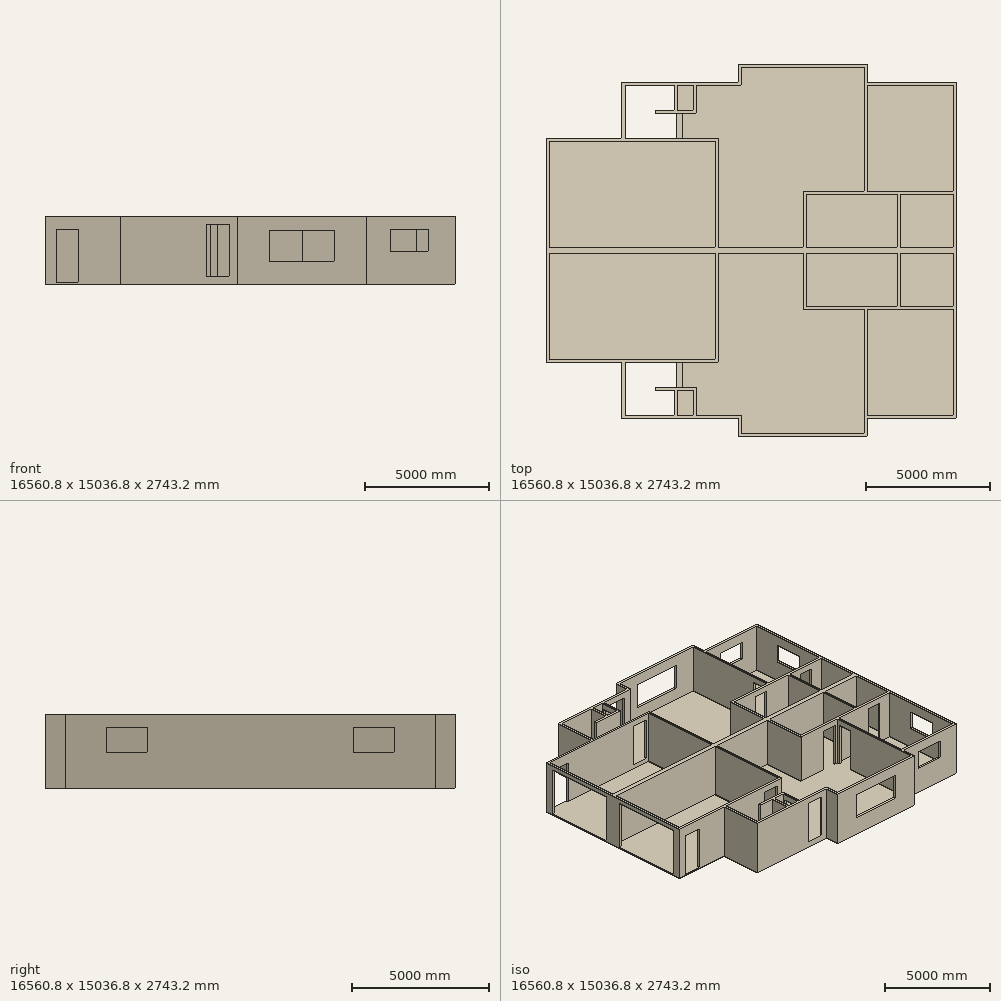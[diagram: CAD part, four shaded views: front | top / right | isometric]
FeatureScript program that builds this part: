
annotation { "Feature Type Name" : "Feature", "Feature Type Description" : "" }
export const myFeature = defineFeature(function(context is Context, id is Id, definition is map)
    precondition{}
    {
        {
            var Q0;
            Q0=qCreatedBy(makeId("Top.planeOp"),FACE);
            var sketch = newSketch(context, id + "F0", { "sketchPlane" : qUnion([Q0])});
            skLineSegment(sketch, "E0", {"start": v(0, 0) * mm, "end": v(16560.8, 0) * mm});
            skLineSegment(sketch, "E1", {"start": v(0, 0) * mm, "end": v(0, 4521.2) * mm});
            skLineSegment(sketch, "E2", {"start": v(0, 4521.2) * mm, "end": v(3048, 4521.2) * mm});
            skLineSegment(sketch, "E3", {"start": v(3048, 4521.2) * mm, "end": v(3048, 6781.8) * mm});
            skLineSegment(sketch, "E4", {"start": v(3048, 6781.8) * mm, "end": v(7747, 6781.8) * mm});
            skLineSegment(sketch, "E5", {"start": v(7747, 6781.8) * mm, "end": v(7747, 7518.4) * mm});
            skLineSegment(sketch, "E6", {"start": v(7747, 7518.4) * mm, "end": v(12979.4, 7518.4) * mm});
            skLineSegment(sketch, "E7", {"start": v(12979.4, 7518.4) * mm, "end": v(12979.4, 6781.8) * mm});
            skLineSegment(sketch, "E8", {"start": v(12979.4, 6781.8) * mm, "end": v(16560.8, 6781.8) * mm});
            skLineSegment(sketch, "E9", {"start": v(16560.8, 6781.8) * mm, "end": v(16560.8, 0) * mm});
            skSolve(sketch);
        }
        {
            var Q0;
            Q0 = qSketchRegion(id + "F0", true);
            extrude(context, id + "F1", {"entities" : qUnion([Q0]), "depth" : 2743.2 * mm});
        }
        {
            var Q0;
            Q0=makeQuery(id+"F1.opExtrude","CAP_FACE",FACE,{"disambiguationData":[OSD([sQuery(id+"F0.wireOp",EDGE,"E0"),sQuery(id+"F0.wireOp",EDGE,"E1"),sQuery(id+"F0.wireOp",EDGE,"E2"),sQuery(id+"F0.wireOp",EDGE,"E3"),sQuery(id+"F0.wireOp",EDGE,"E4"),sQuery(id+"F0.wireOp",EDGE,"E5"),sQuery(id+"F0.wireOp",EDGE,"E6"),sQuery(id+"F0.wireOp",EDGE,"E7"),sQuery(id+"F0.wireOp",EDGE,"E8"),sQuery(id+"F0.wireOp",EDGE,"E9")])],"isStart":false});
            var sketch = newSketch(context, id + "F2", { "sketchPlane" : qUnion([Q0])});
            skLineSegment(sketch, "E10.bottom", {"start": v(127, 4394.2) * mm, "end": v(6832.6, 4394.2) * mm});
            skLineSegment(sketch, "E10.top", {"start": v(127, 127) * mm, "end": v(6832.6, 127) * mm});
            skLineSegment(sketch, "E10.left", {"start": v(127, 4394.2) * mm, "end": v(127, 127) * mm});
            skLineSegment(sketch, "E10.right", {"start": v(6832.6, 4394.2) * mm, "end": v(6832.6, 127) * mm});
            skLineSegment(sketch, "E11.bottom", {"start": v(16433.8, 6654.8) * mm, "end": v(12979.4, 6654.8) * mm});
            skLineSegment(sketch, "E11.top", {"start": v(16433.8, 2387.6) * mm, "end": v(12979.4, 2387.6) * mm});
            skLineSegment(sketch, "E11.left", {"start": v(16433.8, 6654.8) * mm, "end": v(16433.8, 2387.6) * mm});
            skLineSegment(sketch, "E11.right", {"start": v(12979.4, 6654.8) * mm, "end": v(12979.4, 2387.6) * mm});
            skLineSegment(sketch, "E12.bottom", {"start": v(16433.8, 2260.6) * mm, "end": v(14300.2, 2260.6) * mm});
            skLineSegment(sketch, "E12.top", {"start": v(16433.8, 127) * mm, "end": v(14300.2, 127) * mm});
            skLineSegment(sketch, "E12.left", {"start": v(16433.8, 2260.6) * mm, "end": v(16433.8, 127) * mm});
            skLineSegment(sketch, "E12.right", {"start": v(14300.2, 2260.6) * mm, "end": v(14300.2, 127) * mm});
            skLineSegment(sketch, "E13.bottom", {"start": v(14173.2, 127) * mm, "end": v(10515.6, 127) * mm});
            skLineSegment(sketch, "E13.top", {"start": v(14173.2, 2260.6) * mm, "end": v(10515.6, 2260.6) * mm});
            skLineSegment(sketch, "E13.left", {"start": v(14173.2, 127) * mm, "end": v(14173.2, 2260.6) * mm});
            skLineSegment(sketch, "E13.right", {"start": v(10515.6, 127) * mm, "end": v(10515.6, 2260.6) * mm});
            skLineSegment(sketch, "E14", {"start": v(6959.6, 4521.2) * mm, "end": v(6959.6, 127) * mm});
            skLineSegment(sketch, "E15", {"start": v(6959.6, 127) * mm, "end": v(10388.6, 127) * mm});
            skLineSegment(sketch, "E16", {"start": v(10388.6, 127) * mm, "end": v(10388.6, 2387.6) * mm});
            skLineSegment(sketch, "E17", {"start": v(10388.6, 2387.6) * mm, "end": v(12852.4, 2387.6) * mm});
            skLineSegment(sketch, "E18", {"start": v(12852.4, 2387.6) * mm, "end": v(12852.4, 7391.4) * mm});
            skLineSegment(sketch, "E19", {"start": v(12852.4, 7391.4) * mm, "end": v(7874, 7391.4) * mm});
            skLineSegment(sketch, "E20", {"start": v(7874, 7391.4) * mm, "end": v(7874, 6654.8) * mm});
            skLineSegment(sketch, "E21", {"start": v(7874, 6654.8) * mm, "end": v(6045.2, 6654.8) * mm});
            skLineSegment(sketch, "E22", {"start": v(6045.2, 6654.8) * mm, "end": v(6045.2, 5524.5) * mm});
            skLineSegment(sketch, "E23", {"start": v(3175, 6654.8) * mm, "end": v(3175, 4521.2) * mm});
            skLineSegment(sketch, "E24", {"start": v(3175, 4521.2) * mm, "end": v(6959.6, 4521.2) * mm});
            skLineSegment(sketch, "E25", {"start": v(3175, 6654.8) * mm, "end": v(5181.6, 6654.8) * mm});
            skLineSegment(sketch, "E26", {"start": v(6045.2, 5524.5) * mm, "end": v(4394.2, 5524.5) * mm});
            skLineSegment(sketch, "E27", {"start": v(4394.2, 5524.5) * mm, "end": v(4394.2, 5651.5) * mm});
            skLineSegment(sketch, "E28", {"start": v(4394.2, 5651.5) * mm, "end": v(5181.6, 5651.5) * mm});
            skLineSegment(sketch, "E29", {"start": v(5181.6, 5651.5) * mm, "end": v(5181.6, 6654.8) * mm});
            skLineSegment(sketch, "E30.bottom", {"start": v(5308.6, 6654.8) * mm, "end": v(5918.2, 6654.8) * mm});
            skLineSegment(sketch, "E30.top", {"start": v(5308.6, 5651.5) * mm, "end": v(5918.2, 5651.5) * mm});
            skLineSegment(sketch, "E30.left", {"start": v(5308.6, 6654.8) * mm, "end": v(5308.6, 5651.5) * mm});
            skLineSegment(sketch, "E30.right", {"start": v(5918.2, 6654.8) * mm, "end": v(5918.2, 5651.5) * mm});
            skSolve(sketch);
        }
        {
            var Q0;
            Q0 = qSketchRegion(id + "F2", true);
            extrude(context, id + "F3", {"entities" : qUnion([Q0]), "operationType" : NewBodyOperationType.REMOVE, "oppositeDirection" : true, "depth" : 2438.4 * mm});
        }
        {
            var Q0;
            Q0=makeQuery(id+"F3.boolean.opBoolean","COPY",FACE,{"derivedFrom":makeQuery(id+"F3.opExtrude","CAP_FACE",FACE,{"disambiguationData":[OSD([sQuery(id+"F2.wireOp",EDGE,"E10.bottom"),sQuery(id+"F2.wireOp",EDGE,"E10.top"),sQuery(id+"F2.wireOp",EDGE,"E10.left"),sQuery(id+"F2.wireOp",EDGE,"E10.right")])],"isStart":false})});
            var sketch = newSketch(context, id + "F4", { "sketchPlane" : qUnion([Q0])});
            skLineSegment(sketch, "E31.bottom", {"start": v(127, 4394.2) * mm, "end": v(6832.6, 4394.2) * mm});
            skLineSegment(sketch, "E31.top", {"start": v(127, 127) * mm, "end": v(6832.6, 127) * mm});
            skLineSegment(sketch, "E31.left", {"start": v(127, 4394.2) * mm, "end": v(127, 127) * mm});
            skLineSegment(sketch, "E31.right", {"start": v(6832.6, 4394.2) * mm, "end": v(6832.6, 127) * mm});
            skSolve(sketch);
        }
        {
            var Q0;
            Q0 = qSketchRegion(id + "F4", true);
            extrude(context, id + "F5", {"entities" : qUnion([Q0]), "operationType" : NewBodyOperationType.REMOVE, "oppositeDirection" : true, "depth" : 228.6 * mm});
        }
        {
            var Q0;
            Q0=makeQuery(id+"F5.boolean.opBoolean","MERGE",FACE,{"derivedFrom":[makeQuery(id+"F3.boolean.opBoolean","COPY",FACE,{"derivedFrom":makeQuery(id+"F3.opExtrude","SWEPT_FACE",FACE,{"disambiguationData":[OSD([sQuery(id+"F2.wireOp",EDGE,"E10.left")])]})}),makeQuery(id+"F5.opExtrude","SWEPT_FACE",FACE,{"disambiguationData":[OSD([sQuery(id+"F4.wireOp",EDGE,"E31.left")])]})]});
            var sketch = newSketch(context, id + "F6", { "sketchPlane" : qUnion([Q0])});
            skLineSegment(sketch, "E32.bottom", {"start": v(4089.4, 76.2) * mm, "end": v(431.8, 76.2) * mm});
            skLineSegment(sketch, "E32.top", {"start": v(4089.4, 2514.6) * mm, "end": v(431.8, 2514.6) * mm});
            skLineSegment(sketch, "E32.left", {"start": v(4089.4, 76.2) * mm, "end": v(4089.4, 2514.6) * mm});
            skLineSegment(sketch, "E32.right", {"start": v(431.8, 76.2) * mm, "end": v(431.8, 2514.6) * mm});
            skLineSegment(sketch, "E33", {"start": v(2260.6, 2743.2) * mm, "end": v(2260.6, 76.2) * mm, "construction": true});
            skSolve(sketch);
        }
        {
            var Q0;
            Q0 = qSketchRegion(id + "F6", true);
            extrude(context, id + "F7", {"entities" : qUnion([Q0]), "operationType" : NewBodyOperationType.REMOVE, "endBound" : BoundingType.UP_TO_NEXT, "oppositeDirection" : true, "depth" : 25.4 * mm});
        }
        {
            var Q0;
            Q0=makeQuery(id+"F5.boolean.opBoolean","MERGE",FACE,{"derivedFrom":[makeQuery(id+"F3.boolean.opBoolean","COPY",FACE,{"derivedFrom":makeQuery(id+"F3.opExtrude","SWEPT_FACE",FACE,{"disambiguationData":[OSD([sQuery(id+"F2.wireOp",EDGE,"E10.bottom")])]})}),makeQuery(id+"F5.opExtrude","SWEPT_FACE",FACE,{"disambiguationData":[OSD([sQuery(id+"F4.wireOp",EDGE,"E31.bottom")])]})]});
            var sketch = newSketch(context, id + "F8", { "sketchPlane" : qUnion([Q0])});
            skLineSegment(sketch, "E34.bottom", {"start": v(431.8, 76.2) * mm, "end": v(1346.2, 76.2) * mm});
            skLineSegment(sketch, "E34.top", {"start": v(431.8, 2209.8) * mm, "end": v(1346.2, 2209.8) * mm});
            skLineSegment(sketch, "E34.left", {"start": v(431.8, 76.2) * mm, "end": v(431.8, 2209.8) * mm});
            skLineSegment(sketch, "E34.right", {"start": v(1346.2, 76.2) * mm, "end": v(1346.2, 2209.8) * mm});
            skSolve(sketch);
        }
        {
            var Q0;
            Q0 = qSketchRegion(id + "F8", true);
            extrude(context, id + "F9", {"entities" : qUnion([Q0]), "operationType" : NewBodyOperationType.REMOVE, "endBound" : BoundingType.UP_TO_NEXT, "oppositeDirection" : true, "depth" : 25.4 * mm});
        }
        {
            var Q0;
            Q0=makeQuery(id+"F3.boolean.opBoolean","COPY",FACE,{"derivedFrom":makeQuery(id+"F3.opExtrude","SWEPT_FACE",FACE,{"disambiguationData":[OSD([sQuery(id+"F2.wireOp",EDGE,"E24")])]})});
            var sketch = newSketch(context, id + "F10", { "sketchPlane" : qUnion([Q0])});
            skLineSegment(sketch, "E35.bottom", {"start": v(-6680.2, 304.8) * mm, "end": v(-5765.8, 304.8) * mm});
            skLineSegment(sketch, "E35.top", {"start": v(-6680.2, 2438.4) * mm, "end": v(-5765.8, 2438.4) * mm});
            skLineSegment(sketch, "E35.left", {"start": v(-6680.2, 304.8) * mm, "end": v(-6680.2, 2438.4) * mm});
            skLineSegment(sketch, "E35.right", {"start": v(-5765.8, 304.8) * mm, "end": v(-5765.8, 2438.4) * mm});
            skSolve(sketch);
        }
        {
            var Q0;
            Q0 = qSketchRegion(id + "F10", true);
            extrude(context, id + "F11", {"entities" : qUnion([Q0]), "operationType" : NewBodyOperationType.REMOVE, "endBound" : BoundingType.UP_TO_NEXT, "oppositeDirection" : true, "depth" : 25.4 * mm});
        }
        {
            var Q0;
            Q0=makeQuery(id+"F3.boolean.opBoolean","COPY",FACE,{"derivedFrom":makeQuery(id+"F3.opExtrude","SWEPT_FACE",FACE,{"disambiguationData":[OSD([sQuery(id+"F2.wireOp",EDGE,"E26")])]})});
            var sketch = newSketch(context, id + "F12", { "sketchPlane" : qUnion([Q0])});
            skLineSegment(sketch, "E36", {"start": v(5511.8, 304.8) * mm, "end": v(5511.8, 101.6) * mm});
            skLineSegment(sketch, "E37", {"start": v(5511.8, 101.6) * mm, "end": v(5232.4, 101.6) * mm});
            skLineSegment(sketch, "E38", {"start": v(5232.4, 101.6) * mm, "end": v(5232.4, 0) * mm});
            skLineSegment(sketch, "E39", {"start": v(5511.8, 304.8) * mm, "end": v(4394.2, 304.8) * mm});
            skLineSegment(sketch, "E40", {"start": v(4394.2, 304.8) * mm, "end": v(4394.2, 0) * mm});
            skLineSegment(sketch, "E41", {"start": v(4394.2, 0) * mm, "end": v(5232.4, 0) * mm});
            skSolve(sketch);
        }
        {
            var Q0;
            Q0 = qSketchRegion(id + "F12", true);
            extrude(context, id + "F13", {"entities" : qUnion([Q0]), "operationType" : NewBodyOperationType.REMOVE, "depth" : 1003.3 * mm});
        }
        {
            var Q0;
            {var subQ0=sQuery(id+"F2.wireOp",EDGE,"E26");var subQ1=sQuery(id+"F2.wireOp",EDGE,"E23");var subQ2=sQuery(id+"F2.wireOp",EDGE,"E25");var subQ3=sQuery(id+"F2.wireOp",EDGE,"E24");var subQ10=sQuery(id+"F2.wireOp",EDGE,"E27");var subQ11=sQuery(id+"F2.wireOp",EDGE,"E28");var subQ12=sQuery(id+"F2.wireOp",EDGE,"E29");Q0=makeQuery(id+"F13.boolean.opBoolean","SPLIT",FACE,{"disambiguationData":[TD([makeQuery(id+"F3.boolean.opBoolean","COPY",FACE,{"derivedFrom":makeQuery(id+"F3.opExtrude","SWEPT_FACE",FACE,{"disambiguationData":[OSD([subQ1])]})})])],"derivedFrom":makeQuery(id+"F11.boolean.opBoolean","MERGE",FACE,{"derivedFrom":[makeQuery(id+"F3.boolean.opBoolean","COPY",FACE,{"derivedFrom":makeQuery(id+"F3.opExtrude","CAP_FACE",FACE,{"disambiguationData":[OSD([sQuery(id+"F2.wireOp",EDGE,"E14"),sQuery(id+"F2.wireOp",EDGE,"E15"),sQuery(id+"F2.wireOp",EDGE,"E16"),sQuery(id+"F2.wireOp",EDGE,"E17"),sQuery(id+"F2.wireOp",EDGE,"E18"),sQuery(id+"F2.wireOp",EDGE,"E19"),sQuery(id+"F2.wireOp",EDGE,"E20"),sQuery(id+"F2.wireOp",EDGE,"E21"),sQuery(id+"F2.wireOp",EDGE,"E22"),subQ1,subQ3,subQ2,subQ0,subQ10,subQ11,subQ12])],"isStart":false})}),makeQuery(id+"F11.opExtrude","SWEPT_FACE",FACE,{"disambiguationData":[OSD([sQuery(id+"F10.wireOp",EDGE,"E35.bottom")])]})]})});}
            var sketch = newSketch(context, id + "F14", { "sketchPlane" : qUnion([Q0])});
            skLineSegment(sketch, "E42", {"start": v(5181.6, 5651.5) * mm, "end": v(4394.2, 5651.5) * mm});
            skLineSegment(sketch, "E43", {"start": v(4394.2, 5651.5) * mm, "end": v(4394.2, 4521.2) * mm});
            skLineSegment(sketch, "E44", {"start": v(4394.2, 4521.2) * mm, "end": v(3175, 4521.2) * mm});
            skLineSegment(sketch, "E45", {"start": v(3175, 4521.2) * mm, "end": v(3175, 6654.8) * mm});
            skLineSegment(sketch, "E46", {"start": v(3175, 6654.8) * mm, "end": v(5181.6, 6654.8) * mm});
            skLineSegment(sketch, "E47", {"start": v(5181.6, 6654.8) * mm, "end": v(5181.6, 5651.5) * mm});
            skSolve(sketch);
        }
        {
            var Q0;
            Q0 = qSketchRegion(id + "F14", true);
            extrude(context, id + "F15", {"entities" : qUnion([Q0]), "operationType" : NewBodyOperationType.REMOVE, "endBound" : BoundingType.UP_TO_NEXT, "oppositeDirection" : true, "depth" : 25.4 * mm});
        }
        {
            var Q0;
            Q0=makeQuery(id+"F3.boolean.opBoolean","COPY",FACE,{"derivedFrom":makeQuery(id+"F3.opExtrude","SWEPT_FACE",FACE,{"disambiguationData":[OSD([sQuery(id+"F2.wireOp",EDGE,"E21")])]})});
            var sketch = newSketch(context, id + "F16", { "sketchPlane" : qUnion([Q0])});
            skLineSegment(sketch, "E48.bottom", {"start": v(6502.4, 304.8) * mm, "end": v(7416.8, 304.8) * mm});
            skLineSegment(sketch, "E48.top", {"start": v(6502.4, 2438.4) * mm, "end": v(7416.8, 2438.4) * mm});
            skLineSegment(sketch, "E48.left", {"start": v(6502.4, 304.8) * mm, "end": v(6502.4, 2438.4) * mm});
            skLineSegment(sketch, "E48.right", {"start": v(7416.8, 304.8) * mm, "end": v(7416.8, 2438.4) * mm});
            skSolve(sketch);
        }
        {
            var Q0;
            Q0 = qSketchRegion(id + "F16", true);
            extrude(context, id + "F17", {"entities" : qUnion([Q0]), "operationType" : NewBodyOperationType.REMOVE, "endBound" : BoundingType.UP_TO_NEXT, "oppositeDirection" : true, "depth" : 25.4 * mm});
        }
        {
            var Q0;
            Q0=makeQuery(id+"F3.boolean.opBoolean","COPY",FACE,{"derivedFrom":makeQuery(id+"F3.opExtrude","SWEPT_FACE",FACE,{"disambiguationData":[OSD([sQuery(id+"F2.wireOp",EDGE,"E22")])]})});
            var sketch = newSketch(context, id + "F18", { "sketchPlane" : qUnion([Q0])});
            skLineSegment(sketch, "E49.bottom", {"start": v(5765.8, 304.8) * mm, "end": v(6578.6, 304.8) * mm});
            skLineSegment(sketch, "E49.top", {"start": v(5765.8, 2438.4) * mm, "end": v(6578.6, 2438.4) * mm});
            skLineSegment(sketch, "E49.left", {"start": v(5765.8, 304.8) * mm, "end": v(5765.8, 2438.4) * mm});
            skLineSegment(sketch, "E49.right", {"start": v(6578.6, 304.8) * mm, "end": v(6578.6, 2438.4) * mm});
            skSolve(sketch);
        }
        {
            var Q0;
            Q0 = qSketchRegion(id + "F18", true);
            extrude(context, id + "F19", {"entities" : qUnion([Q0]), "operationType" : NewBodyOperationType.REMOVE, "endBound" : BoundingType.UP_TO_NEXT, "oppositeDirection" : true, "depth" : 25.4 * mm});
        }
        {
            var Q0;
            Q0=makeQuery(id+"F3.boolean.opBoolean","COPY",FACE,{"derivedFrom":makeQuery(id+"F3.opExtrude","SWEPT_FACE",FACE,{"disambiguationData":[OSD([sQuery(id+"F2.wireOp",EDGE,"E19")])]})});
            var sketch = newSketch(context, id + "F20", { "sketchPlane" : qUnion([Q0])});
            skLineSegment(sketch, "E50.bottom", {"start": v(9042.4, 2184.4) * mm, "end": v(11684, 2184.4) * mm});
            skLineSegment(sketch, "E50.top", {"start": v(9042.4, 914.4) * mm, "end": v(11684, 914.4) * mm});
            skLineSegment(sketch, "E50.left", {"start": v(9042.4, 2184.4) * mm, "end": v(9042.4, 914.4) * mm});
            skLineSegment(sketch, "E50.right", {"start": v(11684, 2184.4) * mm, "end": v(11684, 914.4) * mm});
            skLineSegment(sketch, "E51", {"start": v(10363.2, 2743.2) * mm, "end": v(10363.2, 304.8) * mm, "construction": true});
            skSolve(sketch);
        }
        {
            var Q0;
            Q0 = qSketchRegion(id + "F20", true);
            extrude(context, id + "F21", {"entities" : qUnion([Q0]), "operationType" : NewBodyOperationType.REMOVE, "endBound" : BoundingType.UP_TO_NEXT, "oppositeDirection" : true, "depth" : 25.4 * mm});
        }
        {
            var Q0;
            Q0=makeQuery(id+"F3.boolean.opBoolean","COPY",FACE,{"derivedFrom":makeQuery(id+"F3.opExtrude","SWEPT_FACE",FACE,{"disambiguationData":[OSD([sQuery(id+"F2.wireOp",EDGE,"E18")])]})});
            var sketch = newSketch(context, id + "F22", { "sketchPlane" : qUnion([Q0])});
            skLineSegment(sketch, "E52.bottom", {"start": v(-2540, 304.8) * mm, "end": v(-3302, 304.8) * mm});
            skLineSegment(sketch, "E52.top", {"start": v(-2540, 2438.4) * mm, "end": v(-3302, 2438.4) * mm});
            skLineSegment(sketch, "E52.left", {"start": v(-2540, 304.8) * mm, "end": v(-2540, 2438.4) * mm});
            skLineSegment(sketch, "E52.right", {"start": v(-3302, 304.8) * mm, "end": v(-3302, 2438.4) * mm});
            skSolve(sketch);
        }
        {
            var Q0;
            Q0 = qSketchRegion(id + "F22", true);
            extrude(context, id + "F23", {"entities" : qUnion([Q0]), "operationType" : NewBodyOperationType.REMOVE, "endBound" : BoundingType.UP_TO_NEXT, "oppositeDirection" : true, "depth" : 25.4 * mm});
        }
        {
            var Q0;
            Q0=makeQuery(id+"F3.boolean.opBoolean","COPY",FACE,{"derivedFrom":makeQuery(id+"F3.opExtrude","SWEPT_FACE",FACE,{"disambiguationData":[OSD([sQuery(id+"F2.wireOp",EDGE,"E17")])]})});
            var sketch = newSketch(context, id + "F24", { "sketchPlane" : qUnion([Q0])});
            skLineSegment(sketch, "E53.bottom", {"start": v(-12700, 304.8) * mm, "end": v(-11938, 304.8) * mm});
            skLineSegment(sketch, "E53.top", {"start": v(-12700, 2438.4) * mm, "end": v(-11938, 2438.4) * mm});
            skLineSegment(sketch, "E53.left", {"start": v(-12700, 304.8) * mm, "end": v(-12700, 2438.4) * mm});
            skLineSegment(sketch, "E53.right", {"start": v(-11938, 304.8) * mm, "end": v(-11938, 2438.4) * mm});
            skSolve(sketch);
        }
        {
            var Q0;
            Q0 = qSketchRegion(id + "F24", true);
            extrude(context, id + "F25", {"entities" : qUnion([Q0]), "operationType" : NewBodyOperationType.REMOVE, "endBound" : BoundingType.UP_TO_NEXT, "oppositeDirection" : true, "depth" : 25.4 * mm});
        }
        {
            var Q0;
            Q0=makeQuery(id+"F3.boolean.opBoolean","COPY",FACE,{"derivedFrom":makeQuery(id+"F3.opExtrude","SWEPT_FACE",FACE,{"disambiguationData":[OSD([sQuery(id+"F2.wireOp",EDGE,"E11.bottom")])]})});
            var sketch = newSketch(context, id + "F26", { "sketchPlane" : qUnion([Q0])});
            skLineSegment(sketch, "E54.bottom", {"start": v(13944.6, 2235.2) * mm, "end": v(15468.6, 2235.2) * mm});
            skLineSegment(sketch, "E54.top", {"start": v(13944.6, 1320.8) * mm, "end": v(15468.6, 1320.8) * mm});
            skLineSegment(sketch, "E54.left", {"start": v(13944.6, 2235.2) * mm, "end": v(13944.6, 1320.8) * mm});
            skLineSegment(sketch, "E54.right", {"start": v(15468.6, 2235.2) * mm, "end": v(15468.6, 1320.8) * mm});
            skLineSegment(sketch, "E55", {"start": v(14706.6, 2743.2) * mm, "end": v(14706.6, 304.8) * mm, "construction": true});
            skSolve(sketch);
        }
        {
            var Q0;
            Q0 = qSketchRegion(id + "F26", true);
            extrude(context, id + "F27", {"entities" : qUnion([Q0]), "operationType" : NewBodyOperationType.REMOVE, "endBound" : BoundingType.UP_TO_NEXT, "oppositeDirection" : true, "depth" : 25.4 * mm});
        }
        {
            var Q0;
            Q0=makeQuery(id+"F3.boolean.opBoolean","COPY",FACE,{"derivedFrom":makeQuery(id+"F3.opExtrude","SWEPT_FACE",FACE,{"disambiguationData":[OSD([sQuery(id+"F2.wireOp",EDGE,"E11.left")])]})});
            var sketch = newSketch(context, id + "F28", { "sketchPlane" : qUnion([Q0])});
            skLineSegment(sketch, "E56", {"start": v(-4521.2, 2743.2) * mm, "end": v(-4521.2, 304.8) * mm, "construction": true});
            skLineSegment(sketch, "E57.bottom", {"start": v(-5283.2, 2235.2) * mm, "end": v(-3759.2, 2235.2) * mm});
            skLineSegment(sketch, "E57.top", {"start": v(-5283.2, 1320.8) * mm, "end": v(-3759.2, 1320.8) * mm});
            skLineSegment(sketch, "E57.left", {"start": v(-5283.2, 2235.2) * mm, "end": v(-5283.2, 1320.8) * mm});
            skLineSegment(sketch, "E57.right", {"start": v(-3759.2, 2235.2) * mm, "end": v(-3759.2, 1320.8) * mm});
            skSolve(sketch);
        }
        {
            var Q0;
            Q0 = qSketchRegion(id + "F28", true);
            extrude(context, id + "F29", {"entities" : qUnion([Q0]), "operationType" : NewBodyOperationType.REMOVE, "endBound" : BoundingType.UP_TO_NEXT, "oppositeDirection" : true, "depth" : 25.4 * mm});
        }
        {
            var Q0;
            Q0=makeQuery(id+"F3.boolean.opBoolean","COPY",FACE,{"derivedFrom":makeQuery(id+"F3.opExtrude","SWEPT_FACE",FACE,{"disambiguationData":[OSD([sQuery(id+"F2.wireOp",EDGE,"E12.bottom")])]})});
            var sketch = newSketch(context, id + "F30", { "sketchPlane" : qUnion([Q0])});
            skLineSegment(sketch, "E58", {"start": v(15367, 2743.2) * mm, "end": v(15367, 304.8) * mm, "construction": true});
            skLineSegment(sketch, "E59.bottom", {"start": v(14986, 304.8) * mm, "end": v(15748, 304.8) * mm});
            skLineSegment(sketch, "E59.top", {"start": v(14986, 2438.4) * mm, "end": v(15748, 2438.4) * mm});
            skLineSegment(sketch, "E59.left", {"start": v(14986, 304.8) * mm, "end": v(14986, 2438.4) * mm});
            skLineSegment(sketch, "E59.right", {"start": v(15748, 304.8) * mm, "end": v(15748, 2438.4) * mm});
            skSolve(sketch);
        }
        {
            var Q0;
            Q0 = qSketchRegion(id + "F30", true);
            extrude(context, id + "F31", {"entities" : qUnion([Q0]), "operationType" : NewBodyOperationType.REMOVE, "endBound" : BoundingType.UP_TO_NEXT, "oppositeDirection" : true, "depth" : 25.4 * mm});
        }
        {
            var Q0;
            Q0=makeQuery(id+"F1.opExtrude","CAP_FACE",FACE,{"disambiguationData":[OSD([sQuery(id+"F0.wireOp",EDGE,"E0"),sQuery(id+"F0.wireOp",EDGE,"E1"),sQuery(id+"F0.wireOp",EDGE,"E2"),sQuery(id+"F0.wireOp",EDGE,"E3"),sQuery(id+"F0.wireOp",EDGE,"E4"),sQuery(id+"F0.wireOp",EDGE,"E5"),sQuery(id+"F0.wireOp",EDGE,"E6"),sQuery(id+"F0.wireOp",EDGE,"E7"),sQuery(id+"F0.wireOp",EDGE,"E8"),sQuery(id+"F0.wireOp",EDGE,"E9")])],"isStart":true});
            var sketch = newSketch(context, id + "F32", { "sketchPlane" : qUnion([Q0])});
            skLineSegment(sketch, "E60", {"start": v(5181.6, -5651.5) * mm, "end": v(5181.6, -6654.8) * mm});
            skLineSegment(sketch, "E61", {"start": v(5181.6, -6654.8) * mm, "end": v(7874, -6654.8) * mm});
            skLineSegment(sketch, "E62", {"start": v(7874, -6654.8) * mm, "end": v(7874, -7391.4) * mm});
            skLineSegment(sketch, "E63", {"start": v(7874, -7391.4) * mm, "end": v(12852.4, -7391.4) * mm});
            skLineSegment(sketch, "E64", {"start": v(12852.4, -7391.4) * mm, "end": v(12852.4, -2387.6) * mm});
            skLineSegment(sketch, "E65", {"start": v(12852.4, -2387.6) * mm, "end": v(6832.6, -2387.6) * mm});
            skLineSegment(sketch, "E66", {"start": v(6832.6, -2387.6) * mm, "end": v(6832.6, -5651.5) * mm});
            skLineSegment(sketch, "E67", {"start": v(6832.6, -5651.5) * mm, "end": v(5181.6, -5651.5) * mm});
            skLineSegment(sketch, "E68.bottom", {"start": v(5740.4, -4521.2) * mm, "end": v(6705.6, -4521.2) * mm});
            skLineSegment(sketch, "E68.top", {"start": v(5740.4, -5524.5) * mm, "end": v(6705.6, -5524.5) * mm});
            skLineSegment(sketch, "E68.left", {"start": v(5740.4, -4521.2) * mm, "end": v(5740.4, -5524.5) * mm});
            skLineSegment(sketch, "E68.right", {"start": v(6705.6, -4521.2) * mm, "end": v(6705.6, -5524.5) * mm});
            skLineSegment(sketch, "E69.bottom", {"start": v(16433.8, -6654.8) * mm, "end": v(12979.4, -6654.8) * mm});
            skLineSegment(sketch, "E69.top", {"start": v(16433.8, -2387.6) * mm, "end": v(12979.4, -2387.6) * mm});
            skLineSegment(sketch, "E69.left", {"start": v(16433.8, -6654.8) * mm, "end": v(16433.8, -2387.6) * mm});
            skLineSegment(sketch, "E69.right", {"start": v(12979.4, -6654.8) * mm, "end": v(12979.4, -2387.6) * mm});
            skLineSegment(sketch, "E70.bottom", {"start": v(16433.8, -127) * mm, "end": v(14300.2, -127) * mm});
            skLineSegment(sketch, "E70.top", {"start": v(16433.8, -2260.6) * mm, "end": v(14300.2, -2260.6) * mm});
            skLineSegment(sketch, "E70.left", {"start": v(16433.8, -127) * mm, "end": v(16433.8, -2260.6) * mm});
            skLineSegment(sketch, "E70.right", {"start": v(14300.2, -127) * mm, "end": v(14300.2, -2260.6) * mm});
            skLineSegment(sketch, "E71.bottom", {"start": v(14173.2, -127) * mm, "end": v(10515.6, -127) * mm});
            skLineSegment(sketch, "E71.top", {"start": v(14173.2, -2260.6) * mm, "end": v(10515.6, -2260.6) * mm});
            skLineSegment(sketch, "E71.left", {"start": v(14173.2, -127) * mm, "end": v(14173.2, -2260.6) * mm});
            skLineSegment(sketch, "E71.right", {"start": v(10515.6, -127) * mm, "end": v(10515.6, -2260.6) * mm});
            skLineSegment(sketch, "E72.bottom", {"start": v(10388.6, -127) * mm, "end": v(6832.6, -127) * mm});
            skLineSegment(sketch, "E72.top", {"start": v(10388.6, -2260.6) * mm, "end": v(6832.6, -2260.6) * mm});
            skLineSegment(sketch, "E72.left", {"start": v(10388.6, -127) * mm, "end": v(10388.6, -2260.6) * mm});
            skLineSegment(sketch, "E72.right", {"start": v(6832.6, -127) * mm, "end": v(6832.6, -2260.6) * mm});
            skSolve(sketch);
        }
        {
            var Q0;
            Q0 = qSketchRegion(id + "F32", true);
            extrude(context, id + "F33", {"entities" : qUnion([Q0]), "operationType" : NewBodyOperationType.REMOVE, "oppositeDirection" : true, "depth" : 101.6 * mm});
        }
        {
            var Q0;
            Q0=makeQuery(id+"F1.opExtrude","SWEPT_BODY",BODY,{"disambiguationData":[OSD([sQuery(id+"F0.wireOp",EDGE,"E0"),sQuery(id+"F0.wireOp",EDGE,"E1"),sQuery(id+"F0.wireOp",EDGE,"E2"),sQuery(id+"F0.wireOp",EDGE,"E3"),sQuery(id+"F0.wireOp",EDGE,"E4"),sQuery(id+"F0.wireOp",EDGE,"E5"),sQuery(id+"F0.wireOp",EDGE,"E6"),sQuery(id+"F0.wireOp",EDGE,"E7"),sQuery(id+"F0.wireOp",EDGE,"E8"),sQuery(id+"F0.wireOp",EDGE,"E9")])]});
            var Q1;
            Q1=qCreatedBy(makeId("Front.planeOp"),FACE);
            mirror(context, id + "F34", {"operationType" : NewBodyOperationType.ADD, "entities" : qUnion([Q0]), "mirrorPlane" : qUnion([Q1])});
        }
    });
